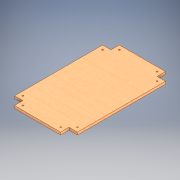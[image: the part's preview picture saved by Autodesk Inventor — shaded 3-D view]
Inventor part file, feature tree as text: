
AUTODESK INVENTOR PART (.ipt)
format: ipt  version: 2020 (Build 240168000, 168)  size: 141,824 bytes
history: native  units: mm
features: extrude x1, sketch x1
ambient origin geometry x8: Origin, YZ Plane, XZ Plane, XY Plane, X Axis, Y Axis, Z Axis, Center Point
bodies: Solide1 (feature_tree)
feature tree (2):
  extrude  "Extrusion1"  Depth=150.0mm
  sketch  "Esquisse1"
